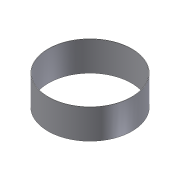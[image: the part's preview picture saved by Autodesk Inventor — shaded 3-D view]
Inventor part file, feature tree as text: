
AUTODESK INVENTOR PART (.ipt)
format: ipt  version: 2012 (Build 160160000, 160)  size: 78,848 bytes
history: native  units: in
note: dims shown in document units (in); Inventor stores cm internally (conversion verified against a paired STEP export)
features: extrude x1, sketch x1
ambient origin geometry x8: Origin, YZ Plane, XZ Plane, XY Plane, X Axis, Y Axis, Z Axis, Center Point
bodies: Solid1 (feature_tree)
feature tree (2):
  extrude  "Extrusion1"  Depth=11.375in
  sketch  "Sketch2"  dims[d0=11.25in d1=11.375in d2=4.0in d3=0.0in]
